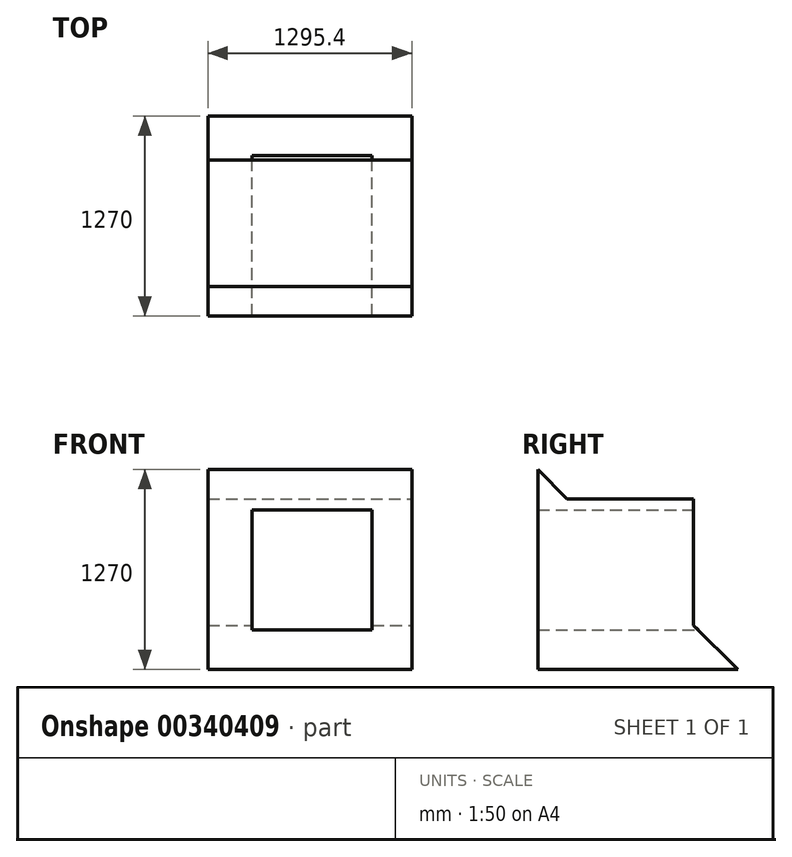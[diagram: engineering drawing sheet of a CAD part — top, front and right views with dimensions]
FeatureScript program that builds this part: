
annotation { "Feature Type Name" : "Feature", "Feature Type Description" : "" }
export const myFeature = defineFeature(function(context is Context, id is Id, definition is map)
    precondition{}
    {
        {
            var Q0;
            Q0=qCreatedBy(makeId("Front.planeOp"),FACE);
            var sketch = newSketch(context, id + "F0", { "sketchPlane" : qUnion([Q0])});
            skLineSegment(sketch, "E0", {"start": v(0, 0) * mm, "end": v(0, 1270) * mm});
            skLineSegment(sketch, "E1", {"start": v(0, 1270) * mm, "end": v(1270, 1270) * mm});
            skLineSegment(sketch, "E2", {"start": v(1270, 1270) * mm, "end": v(1270, 0) * mm});
            skLineSegment(sketch, "E3", {"start": v(1270, 0) * mm, "end": v(0, 0) * mm});
            skLineSegment(sketch, "E4", {"start": v(255.76, 1012.18) * mm, "end": v(255.76, 250.18) * mm});
            skLineSegment(sketch, "E5", {"start": v(255.76, 250.18) * mm, "end": v(1017.76, 250.18) * mm});
            skLineSegment(sketch, "E6", {"start": v(1017.76, 250.18) * mm, "end": v(1017.76, 1012.18) * mm});
            skLineSegment(sketch, "E7", {"start": v(1017.76, 1012.18) * mm, "end": v(255.76, 1012.18) * mm});
            skSolve(sketch);
        }
        {
            var Q0;
            Q0 = qSketchRegion(id + "F0", true);
            extrude(context, id + "F1", {"entities" : qUnion([Q0]), "depth" : 1270 * mm});
        }
        {
            var Q0;
            Q0=makeQuery(id+"F1.opExtrude","SWEPT_FACE",FACE,{"disambiguationData":[OSD([sQuery(id+"F0.wireOp",EDGE,"E2")])]});
            var sketch = newSketch(context, id + "F2", { "sketchPlane" : qUnion([Q0])});
            skLineSegment(sketch, "E8", {"start": v(-1270, 1270) * mm, "end": v(0, 0) * mm});
            skLineSegment(sketch, "E9", {"start": v(0, 0) * mm, "end": v(-1270, 0) * mm});
            skLineSegment(sketch, "E10", {"start": v(-1270, 0) * mm, "end": v(-1270, 1270) * mm});
            skLineSegment(sketch, "E11", {"start": v(-1083.54, 1083.54) * mm, "end": v(-280.4, 1083.54) * mm});
            skLineSegment(sketch, "E12", {"start": v(-280.4, 1083.54) * mm, "end": v(-280.4, 280.4) * mm});
            skLineSegment(sketch, "E13", {"start": v(-280.4, 280.4) * mm, "end": v(-1083.54, 1083.54) * mm});
            skSolve(sketch);
        }
        {
            var Q0;
            Q0=makeQuery(id+"F1.opExtrude","SWEPT_FACE",FACE,{"disambiguationData":[OSD([sQuery(id+"F0.wireOp",EDGE,"E1")])]});
            var sketch = newSketch(context, id + "F3", { "sketchPlane" : qUnion([Q0])});
            skLineSegment(sketch, "E14.bottom", {"start": v(234.94, -930.75) * mm, "end": v(996.94, -930.75) * mm});
            skLineSegment(sketch, "E14.top", {"start": v(234.94, -168.75) * mm, "end": v(996.94, -168.75) * mm});
            skLineSegment(sketch, "E14.left", {"start": v(234.94, -930.75) * mm, "end": v(234.94, -168.75) * mm});
            skLineSegment(sketch, "E14.right", {"start": v(996.94, -930.75) * mm, "end": v(996.94, -168.75) * mm});
            skSolve(sketch);
        }
        {
            var Q0;
            Q0 = qSketchRegion(id + "F3", true);
            extrude(context, id + "F4", {"entities" : qUnion([Q0]), "operationType" : NewBodyOperationType.REMOVE, "endBound" : BoundingType.SYMMETRIC, "depth" : 25.4 * mm});
        }
        {
            var Q0;
            {var subQ0=sQuery(id+"F2.wireOp",EDGE,"E11");Q0=makeQuery(id+"F2.imprint","IMPRINT",FACE,{"disambiguationData":[TD([[makeQuery(id+"F2.imprint","IMPRINT",EDGE,{"derivedFrom":subQ0}),1.0]])]});}
            extrude(context, id + "F5", {"entities" : qUnion([Q0]), "operationType" : NewBodyOperationType.REMOVE, "endBound" : BoundingType.THROUGH_ALL, "oppositeDirection" : true, "depth" : 25.4 * mm});
        }
        {
            var Q0;
            Q0=makeQuery(id+"F1.opExtrude","SWEPT_FACE",FACE,{"disambiguationData":[OSD([sQuery(id+"F0.wireOp",EDGE,"E0")])]});
            extrude(context, id + "F6", {"entities" : qUnion([Q0]), "operationType" : NewBodyOperationType.ADD, "depth" : 25.4 * mm});
        }
    });
